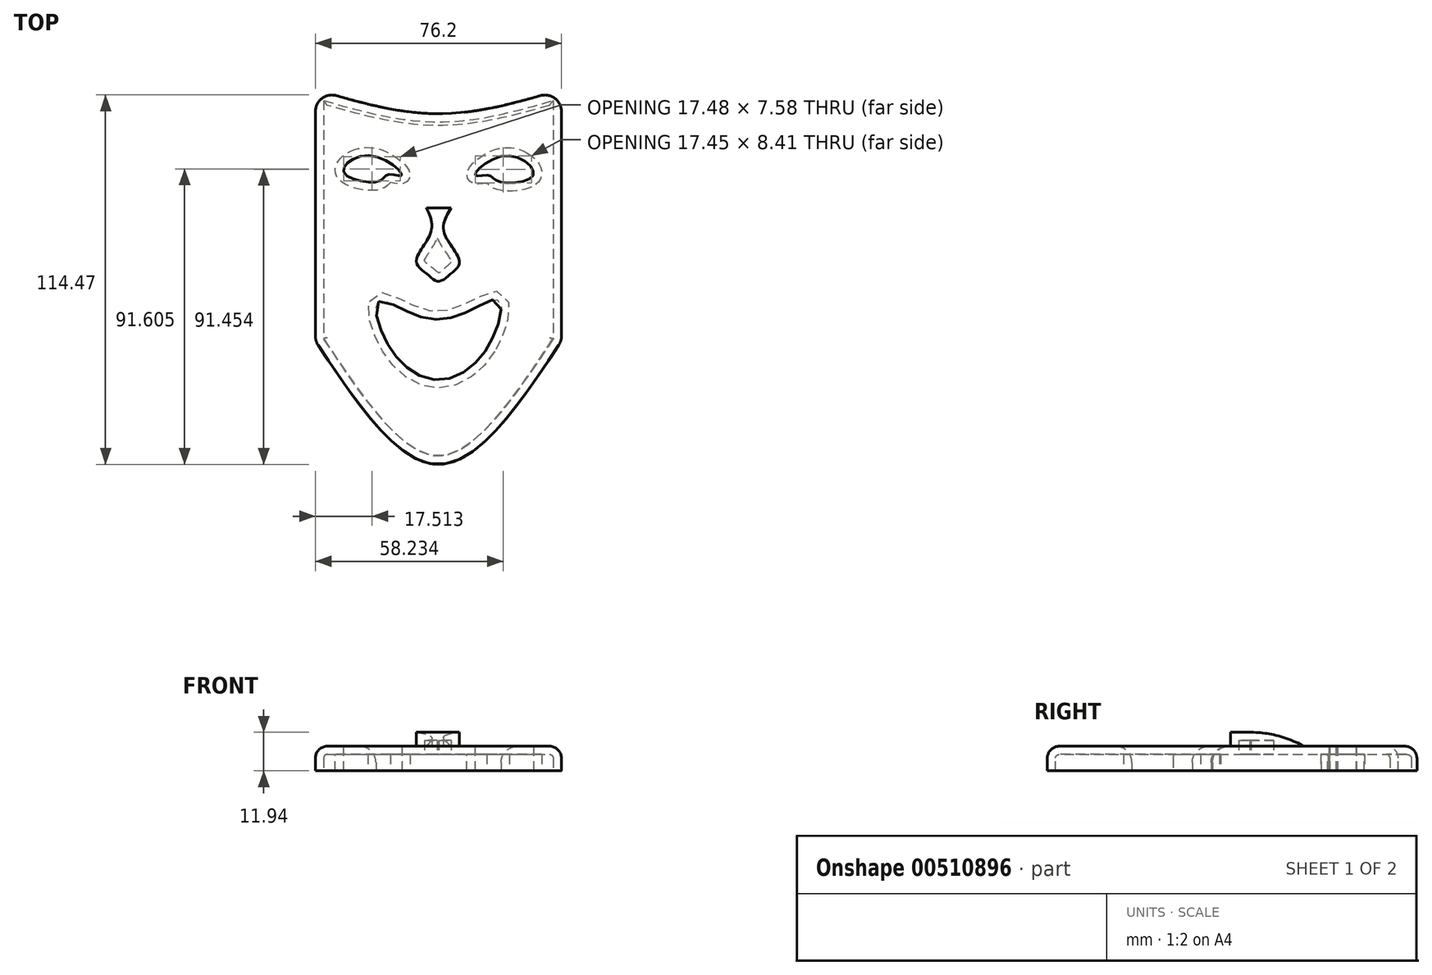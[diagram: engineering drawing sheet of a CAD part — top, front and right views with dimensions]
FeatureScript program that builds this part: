
annotation { "Feature Type Name" : "Feature", "Feature Type Description" : "" }
export const myFeature = defineFeature(function(context is Context, id is Id, definition is map)
    precondition{}
    {
        {
            var Q0;
            Q0=qCreatedBy(makeId("Top.planeOp"),FACE);
            var sketch = newSketch(context, id + "F0", { "sketchPlane" : qUnion([Q0])});
            skLineSegment(sketch, "E0", {"start": v(38.1, 44.28) * mm, "end": v(38.1, -33.7) * mm});
            skLineSegment(sketch, "E1", {"start": v(-38.1, 44.28) * mm, "end": v(-38.1, -33.7) * mm});
            skFitSpline(sketch, "E2", {"points": [v(-38.1, -33.7) * mm, v(0, -71.9) * mm, v(38.1, -33.7) * mm], "startDerivative": vector(76.2, -114.57) * mm, "endDerivative": vector(76.2, 114.57) * mm});
            skFitSpline(sketch, "E3", {"points": [v(-38.1, 44.28) * mm, v(0, 36.78) * mm, v(38.1, 44.28) * mm], "startDerivative": vector(76.2, -22.5) * mm, "endDerivative": vector(76.2, 22.5) * mm});
            skFitSpline(sketch, "E4", {"points": [v(-29.33, 18.75) * mm, v(-21, 23.76) * mm, v(-11.4, 17.72) * mm, v(-15.58, 17.92) * mm, v(-18.5, 15.84) * mm, v(-29.33, 18.75) * mm]});
            skPoint(sketch, "E5", {"position": v(-21, 39.57) * mm});
            skPoint(sketch, "E6", {"position": v(21, 39.57) * mm});
            skPoint(sketch, "E7", {"position": v(-38.1, 18.75) * mm});
            skPoint(sketch, "E8", {"position": v(-18.5, -60.58) * mm});
            skPoint(sketch, "E9", {"position": v(-15.58, -63.62) * mm});
            skPoint(sketch, "E10", {"position": v(15.58, -63.62) * mm});
            skPoint(sketch, "E11", {"position": v(18.5, -60.58) * mm});
            skPoint(sketch, "E12", {"position": v(38.1, 18.75) * mm});
            skPoint(sketch, "E13", {"position": v(-11.4, 37.69) * mm});
            skPoint(sketch, "E14", {"position": v(11.4, 37.69) * mm});
            skPoint(sketch, "E15", {"position": v(-29.33, 41.73) * mm});
            skPoint(sketch, "E16", {"position": v(29.33, 41.73) * mm});
            skFitSpline(sketch, "E17", {"points": [v(11.4, 17.72) * mm, v(21, 23.76) * mm, v(29.33, 17.72) * mm, v(18.5, 15.84) * mm, v(15.58, 17.72) * mm, v(11.4, 17.72) * mm]});
            skFitSpline(sketch, "E18", {"points": [v(-18.5, -21.32) * mm, v(0, -27) * mm, v(18.5, -20.92) * mm, v(15.27, -35.54) * mm, v(0, -45.7) * mm, v(-14.99, -35.74) * mm, v(-18.5, -21.32) * mm]});
            skSolve(sketch);
        }
        {
            var Q0;
            Q0=makeQuery(id+"F0.imprint","IMPRINT",FACE,{"disambiguationData":[TD([[makeQuery(id+"F0.imprint","IMPRINT",EDGE,{"derivedFrom":sQuery(id+"F0.wireOp",EDGE,"E0")}),-1.0]])]});
            var Q1;
            {var subQ1=sQuery(id+"F0.wireOp",EDGE,"E1");Q1=makeQuery(id+"F0.imprint","IMPRINT",FACE,{"disambiguationData":[TD([[makeQuery(id+"F0.imprint","IMPRINT",EDGE,{"derivedFrom":subQ1}),1.0]])]});}
            extrude(context, id + "F1", {"entities" : qUnion([Q0, Q1]), "depth" : 7.62 * mm});
        }
        {
            var Q0;
            Q0=qCreatedBy(makeId("Top.planeOp"),FACE);
            var sketch = newSketch(context, id + "F2", { "sketchPlane" : qUnion([Q0])});
            skPoint(sketch, "E19", {"position": v(0, 7.57) * mm});
            skPoint(sketch, "E20", {"position": v(3.91, 7.57) * mm});
            skPoint(sketch, "E21", {"position": v(-3.66, 7.57) * mm});
            skPoint(sketch, "E22", {"position": v(-2.36, 0) * mm});
            skPoint(sketch, "E23", {"position": v(1.75, 0) * mm});
            skPoint(sketch, "E24", {"position": v(0, -15.14) * mm});
            skPoint(sketch, "E25", {"position": v(3.91, -12.76) * mm});
            skPoint(sketch, "E26", {"position": v(-3.66, -12.76) * mm});
            skPoint(sketch, "E27", {"position": v(-6.9, -8.87) * mm});
            skPoint(sketch, "E28", {"position": v(6.5, -8.87) * mm});
            skFitSpline(sketch, "E29", {"points": [v(-3.66, 7.57) * mm, v(-2.36, 0) * mm, v(-6.9, -8.87) * mm, v(-3.66, -12.76) * mm, v(0, -15.14) * mm, v(3.91, -12.76) * mm, v(6.5, -8.87) * mm, v(1.75, 0) * mm, v(3.91, 7.57) * mm], "startDerivative": vector(24.14, -53.97) * mm, "endDerivative": vector(31.94, 53.32) * mm});
            skLineSegment(sketch, "E30", {"start": v(-3.66, 7.57) * mm, "end": v(3.91, 7.57) * mm});
            skSolve(sketch);
        }
        {
            var Q0;
            Q0 = qSketchRegion(id + "F2", true);
            extrude(context, id + "F3", {"entities" : qUnion([Q0]), "operationType" : NewBodyOperationType.ADD, "depth" : 11.94 * mm});
        }
        {
            var Q0;
            Q0=makeQuery(id+"F1.opExtrude","CAP_EDGE",EDGE,{"disambiguationData":[OSD([sQuery(id+"F0.wireOp",EDGE,"E0")])],"isStart":false});
            var Q1;
            Q1=makeQuery(id+"F1.opExtrude","CAP_EDGE",EDGE,{"disambiguationData":[OSD([sQuery(id+"F0.wireOp",EDGE,"E2")])],"isStart":false});
            var Q2;
            Q2=makeQuery(id+"F1.opExtrude","CAP_EDGE",EDGE,{"disambiguationData":[OSD([sQuery(id+"F0.wireOp",EDGE,"E1")])],"isStart":false});
            var Q3;
            Q3=makeQuery(id+"F1.opExtrude","CAP_EDGE",EDGE,{"disambiguationData":[OSD([sQuery(id+"F0.wireOp",EDGE,"E3")])],"isStart":false});
            fillet(context, id + "F4", {"entities" : qUnion([Q0, Q1, Q2, Q3]), "radius" : 3.68 * mm, "tangentPropagation" : true, "allowEdgeOverflow" : false});
        }
        {
            var Q0;
            Q0=makeQuery(id+"F1.opExtrude","CAP_FACE",FACE,{"disambiguationData":[OSD([sQuery(id+"F0.wireOp",EDGE,"E0"),sQuery(id+"F0.wireOp",EDGE,"E1"),sQuery(id+"F0.wireOp",EDGE,"E2"),sQuery(id+"F0.wireOp",EDGE,"E3"),sQuery(id+"F0.wireOp",EDGE,"E4"),sQuery(id+"F0.wireOp",EDGE,"E17"),sQuery(id+"F0.wireOp",EDGE,"E18")])],"isStart":true});
            shell(context, id + "F5", {"entities" : qUnion([Q0]), "thickness" : 2.54 * mm});
        }
        {
            var Q0;
            Q0=makeQuery(id+"F4.opFillet","BLEND_EDGE",EDGE,{"blendedFrom":[makeQuery(id+"F1.opExtrude","CAP_EDGE",EDGE,{"disambiguationData":[OSD([sQuery(id+"F0.wireOp",EDGE,"E0")])],"isStart":false}),makeQuery(id+"F1.opExtrude","CAP_EDGE",EDGE,{"disambiguationData":[OSD([sQuery(id+"F0.wireOp",EDGE,"E3")])],"isStart":false})],"blendedInto":[]});
            var Q1;
            Q1=makeQuery(id+"F4.opFillet","BLEND_EDGE",EDGE,{"blendedFrom":[makeQuery(id+"F1.opExtrude","CAP_EDGE",EDGE,{"disambiguationData":[OSD([sQuery(id+"F0.wireOp",EDGE,"E1")])],"isStart":false}),makeQuery(id+"F1.opExtrude","CAP_EDGE",EDGE,{"disambiguationData":[OSD([sQuery(id+"F0.wireOp",EDGE,"E3")])],"isStart":false})],"blendedInto":[]});
            var Q2;
            Q2=makeQuery(id+"F4.opFillet","BLEND_EDGE",EDGE,{"blendedFrom":[makeQuery(id+"F1.opExtrude","CAP_EDGE",EDGE,{"disambiguationData":[OSD([sQuery(id+"F0.wireOp",EDGE,"E0")])],"isStart":false}),makeQuery(id+"F1.opExtrude","CAP_EDGE",EDGE,{"disambiguationData":[OSD([sQuery(id+"F0.wireOp",EDGE,"E2")])],"isStart":false})],"blendedInto":[]});
            var Q3;
            Q3=makeQuery(id+"F4.opFillet","BLEND_EDGE",EDGE,{"blendedFrom":[makeQuery(id+"F1.opExtrude","CAP_EDGE",EDGE,{"disambiguationData":[OSD([sQuery(id+"F0.wireOp",EDGE,"E1")])],"isStart":false}),makeQuery(id+"F1.opExtrude","CAP_EDGE",EDGE,{"disambiguationData":[OSD([sQuery(id+"F0.wireOp",EDGE,"E2")])],"isStart":false})],"blendedInto":[]});
            fillet(context, id + "F6", {"entities" : qUnion([Q0, Q1, Q2, Q3]), "radius" : 5.08 * mm, "tangentPropagation" : true, "allowEdgeOverflow" : false});
        }
        {
            var Q0;
            Q0=makeQuery(id+"F3.opExtrude","CAP_EDGE",EDGE,{"disambiguationData":[OSD([sQuery(id+"F2.wireOp",EDGE,"E30")])],"isStart":false});
            fillet(context, id + "F7", {"entities" : qUnion([Q0]), "radius" : 33.48 * mm, "tangentPropagation" : true, "allowEdgeOverflow" : false});
        }
        {
            var Q0;
            Q0=makeQuery(id+"F1.opExtrude","CAP_EDGE",EDGE,{"disambiguationData":[OSD([sQuery(id+"F0.wireOp",EDGE,"E18")])],"isStart":false});
            fillet(context, id + "F8", {"entities" : qUnion([Q0]), "radius" : 5.08 * mm, "tangentPropagation" : true, "allowEdgeOverflow" : false});
        }
    });
